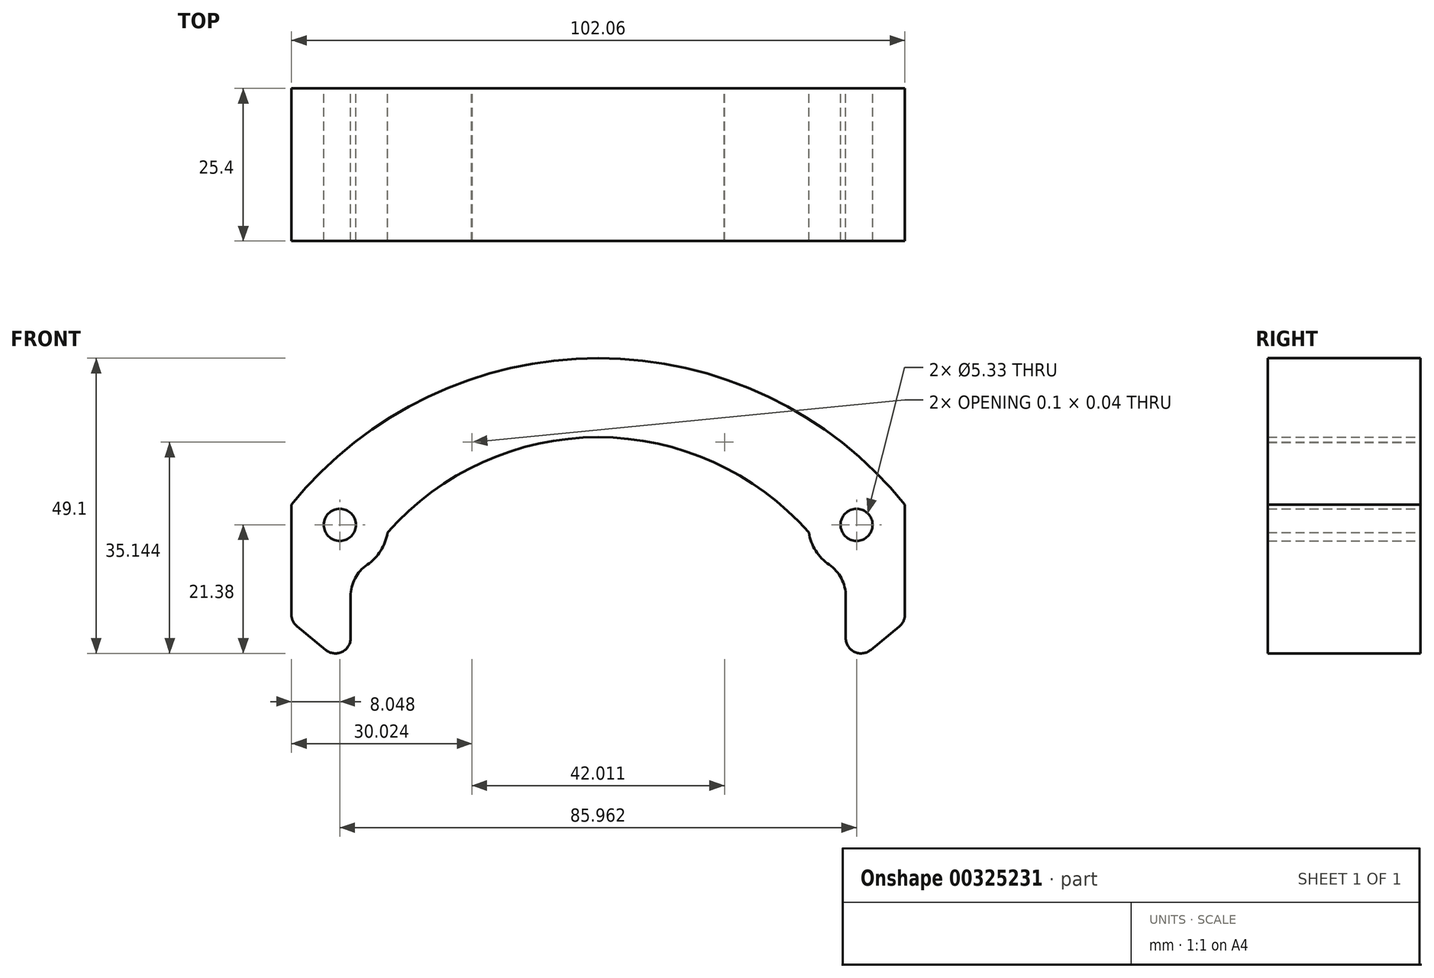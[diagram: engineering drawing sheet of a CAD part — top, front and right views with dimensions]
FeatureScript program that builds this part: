
annotation { "Feature Type Name" : "Feature", "Feature Type Description" : "" }
export const myFeature = defineFeature(function(context is Context, id is Id, definition is map)
    precondition{}
    {
        {
            var Q0;
            Q0=qCreatedBy(makeId("Front.planeOp"),FACE);
            var sketch = newSketch(context, id + "F0", { "sketchPlane" : qUnion([Q0])});
            skLineSegment(sketch, "E0", {"start": v(-112.3, 51.95) * mm, "end": v(-112.3, 33.62) * mm});
            skPoint(sketch, "E1.visualSharp", {"position": v(-98.44, 54.75) * mm});
            skPoint(sketch, "E2.visualSharp", {"position": v(-24.12, 54.75) * mm});
            skCircle(sketch, "E3", {"center": v(-104.26, 48.56) * mm, "radius": 2.67 * mm});
            skArc(sketch, "E4", {"start": v(-99.7, 41.92) * mm, "mid": v(-97.46, 44.25) * mm, "end": v(-96.32, 47.28) * mm});
            skLineSegment(sketch, "E5.MirrorCS", {"start": v(-10.25, 51.95) * mm, "end": v(-10.25, 33.62) * mm});
            skArc(sketch, "E6.MirrorC", {"start": v(-22.85, 41.92) * mm, "mid": v(-25.1, 44.25) * mm, "end": v(-26.24, 47.28) * mm});
            skCircle(sketch, "E7.MirrorC", {"center": v(-18.3, 48.56) * mm, "radius": 2.67 * mm});
            skArc(sketch, "E8", {"start": v(-10.25, 51.95) * mm, "mid": v(-61.28, 76.28) * mm, "end": v(-112.3, 51.95) * mm});
            skArc(sketch, "E9.trimOffspring", {"start": v(-40.23, 62.3) * mm, "mid": v(-40.28, 62.32) * mm, "end": v(-40.32, 62.34) * mm});
            skLineSegment(sketch, "E10", {"start": v(-102.47, 36.69) * mm, "end": v(-102.47, 29.72) * mm});
            skLineSegment(sketch, "E11", {"start": v(-20.1, 36.69) * mm, "end": v(-20.1, 29.72) * mm});
            skPoint(sketch, "E12.visualSharp", {"position": v(-102.47, 40.71) * mm});
            skArc(sketch, "E12.filletArc", {"start": v(-99.7, 41.92) * mm, "mid": v(-101.74, 39.65) * mm, "end": v(-102.47, 36.69) * mm});
            skPoint(sketch, "E13.visualSharp", {"position": v(-97.57, 53.02) * mm});
            skPoint(sketch, "E14.visualSharp", {"position": v(-25, 53.02) * mm});
            skPoint(sketch, "E15.visualSharp", {"position": v(-20.1, 40.71) * mm});
            skArc(sketch, "E15.filletArc", {"start": v(-20.1, 36.69) * mm, "mid": v(-20.83, 39.65) * mm, "end": v(-22.85, 41.92) * mm});
            skPoint(sketch, "E16.orphan", {"position": v(-96.32, 49.84) * mm});
            skArc(sketch, "E17", {"start": v(-82.24, 62.34) * mm, "mid": v(-82.29, 62.32) * mm, "end": v(-82.34, 62.3) * mm});
            skArc(sketch, "E18.MirrorCS", {"start": v(-40.32, 62.34) * mm, "mid": v(-40.28, 62.32) * mm, "end": v(-40.23, 62.3) * mm});
            skArc(sketch, "E19", {"start": v(-26.24, 47.28) * mm, "mid": v(-61.28, 63.14) * mm, "end": v(-96.32, 47.28) * mm});
            skLineSegment(sketch, "E20", {"start": v(-111.38, 31.66) * mm, "end": v(-106.62, 27.75) * mm});
            skLineSegment(sketch, "E21.MirrorCS", {"start": v(-11.18, 31.66) * mm, "end": v(-15.94, 27.75) * mm});
            skPoint(sketch, "E22.visualSharp", {"position": v(-102.47, 24.35) * mm});
            skArc(sketch, "E22.filletArc", {"start": v(-106.62, 27.75) * mm, "mid": v(-103.92, 27.42) * mm, "end": v(-102.47, 29.72) * mm});
            skPoint(sketch, "E23.visualSharp", {"position": v(-112.3, 32.42) * mm});
            skArc(sketch, "E23.filletArc", {"start": v(-112.3, 33.62) * mm, "mid": v(-112.07, 32.54) * mm, "end": v(-111.38, 31.66) * mm});
            skPoint(sketch, "E24.visualSharp", {"position": v(-20.1, 24.35) * mm});
            skArc(sketch, "E24.filletArc", {"start": v(-20.1, 29.72) * mm, "mid": v(-18.64, 27.42) * mm, "end": v(-15.94, 27.75) * mm});
            skPoint(sketch, "E25.visualSharp", {"position": v(-10.25, 32.42) * mm});
            skArc(sketch, "E25.filletArc", {"start": v(-11.18, 31.66) * mm, "mid": v(-10.5, 32.54) * mm, "end": v(-10.25, 33.62) * mm});
            skSolve(sketch);
        }
        {
            var Q0;
            Q0=makeQuery(id+"F0.imprint","IMPRINT",FACE,{"disambiguationData":[TD([[makeQuery(id+"F0.imprint","IMPRINT",EDGE,{"derivedFrom":sQuery(id+"F0.wireOp",EDGE,"E0")}),1.0]])]});
            extrude(context, id + "F1", {"entities" : qUnion([Q0]), "depth" : 25.4 * mm});
        }
    });
